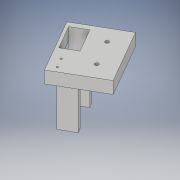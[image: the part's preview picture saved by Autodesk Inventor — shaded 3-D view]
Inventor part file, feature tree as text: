
AUTODESK INVENTOR PART (.ipt)
format: ipt  version: 2017 (Build 210142000, 142)  size: 240,640 bytes
history: native  units: in
note: dims shown in document units (in); Inventor stores cm internally (conversion verified against a paired STEP export)
features: extrude x7, sketch x7, projected_geometry x7, imported_body x1
ambient origin geometry x8: Origin, YZ Plane, XZ Plane, XY Plane, X Axis, Y Axis, Z Axis, Center Point
bodies: Solid1 (feature_tree)
feature tree (22):
  extrude  "Extrusion1"  Depth=0.3937in TaperAngle=0.0deg
  extrude  "Extrusion2"  Depth=0.3937in TaperAngle=0.0deg
  extrude  "Extrusion4"  Depth=0.3937in TaperAngle=0.0deg
  extrude  "Extrusion5"  Depth=0.3937in TaperAngle=0.0deg
  extrude  "Extrusion6"  Depth=0.188in
  extrude  "limit switch"  Depth=0.125in
  extrude  "Extrusion8"  Depth=0.3937in
  sketch  "Sketch1"  dims[d0=1.25in d1=0.3937in d2=0.0in]
  projected_geometry  "Projected Loop1"
  sketch  "Sketch2"  dims[d3=0.125in d4=0.3937in d5=0.0in]
  sketch  "Sketch4"  dims[d9=0.4331in d10=0.3937in d11=0.0in]
  projected_geometry  "Projected Loop3"
  sketch  "Sketch5"  dims[d12=0.3937in d13=0.3937in d14=0.0in]
  projected_geometry  "Projected Loop4"
  sketch  "Sketch6"  dims[d15=0.765in d16=0.188in]
  projected_geometry  "Projected Loop5"
  sketch  "Sketch7"  dims[d17=0.5in d18=0.125in]
  projected_geometry  "Projected Loop6"
  sketch  "Sketch9"  dims[d19=0.3937in d20=0.0in d21=0.276in d22=0.2in d23=0.575in d24=0.063in d25=0.3937in d26=0.0in d27=2.0in d28=0.0in]
  projected_geometry  "Projected Loop8"
  projected_geometry  "Projected Loop9"
  imported_body  "Base1"
